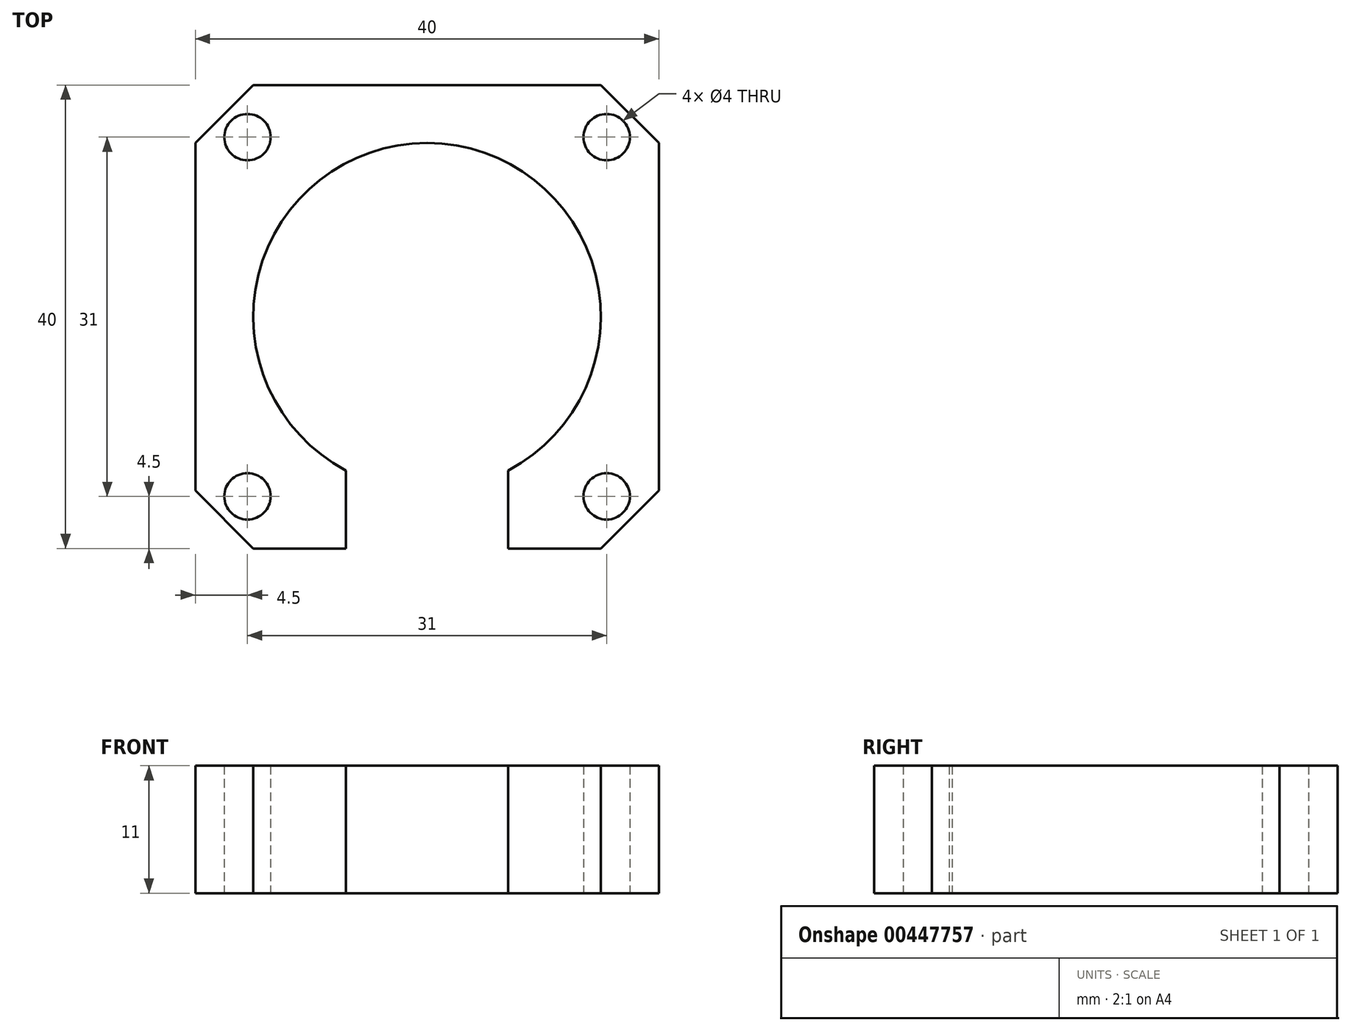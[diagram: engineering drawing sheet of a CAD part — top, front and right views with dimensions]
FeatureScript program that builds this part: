
annotation { "Feature Type Name" : "Feature", "Feature Type Description" : "" }
export const myFeature = defineFeature(function(context is Context, id is Id, definition is map)
    precondition{}
    {
        {
            var Q0;
            Q0=qCreatedBy(makeId("Top.planeOp"),FACE);
            var sketch = newSketch(context, id + "F0", { "sketchPlane" : qUnion([Q0])});
            skLineSegment(sketch, "E0.bottom", {"start": v(20, 20) * mm, "end": v(-20, 20) * mm});
            skLineSegment(sketch, "E0.top", {"start": v(20, -20) * mm, "end": v(-20, -20) * mm});
            skLineSegment(sketch, "E0.left", {"start": v(20, 20) * mm, "end": v(20, -20) * mm});
            skLineSegment(sketch, "E0.right", {"start": v(-20, 20) * mm, "end": v(-20, -20) * mm});
            skPoint(sketch, "E0.middle", {"position": v(0, 0) * mm});
            skCircle(sketch, "E1", {"center": v(15.5, 15.5) * mm, "radius": 2 * mm});
            skCircle(sketch, "E2", {"center": v(-15.5, 15.5) * mm, "radius": 2 * mm});
            skCircle(sketch, "E3", {"center": v(15.5, -15.5) * mm, "radius": 2 * mm});
            skCircle(sketch, "E4", {"center": v(-15.5, -15.5) * mm, "radius": 2 * mm});
            skCircle(sketch, "E5", {"center": v(0, 0) * mm, "radius": 15 * mm});
            skLineSegment(sketch, "E6", {"start": v(0, 0) * mm, "end": v(7, 0) * mm});
            skLineSegment(sketch, "E7", {"start": v(7, 0) * mm, "end": v(7, -20) * mm});
            skLineSegment(sketch, "E8", {"start": v(7, -20) * mm, "end": v(-7, -20) * mm});
            skLineSegment(sketch, "E9", {"start": v(-7, -20) * mm, "end": v(-7, 0) * mm});
            skLineSegment(sketch, "E10", {"start": v(-7, 0) * mm, "end": v(0, 0) * mm});
            skSolve(sketch);
        }
        {
            var Q0;
            Q0=makeQuery(id+"F0.imprint","IMPRINT",FACE,{"disambiguationData":[TD([[makeQuery(id+"F0.imprint","IMPRINT",EDGE,{"derivedFrom":sQuery(id+"F0.wireOp",EDGE,"E0.bottom")}),1.0]])]});
            extrude(context, id + "F1", {"entities" : qUnion([Q0]), "depth" : 11 * mm});
        }
        {
            var Q0;
            Q0=makeQuery(id+"F1.opExtrude","SWEPT_EDGE",EDGE,{"disambiguationData":[OSD([sQuery(id+"F0.wireOp",EDGE,"E0.top"),sQuery(id+"F0.wireOp",EDGE,"E0.right")])]});
            var Q1;
            Q1=makeQuery(id+"F1.opExtrude","SWEPT_EDGE",EDGE,{"disambiguationData":[OSD([sQuery(id+"F0.wireOp",EDGE,"E0.bottom"),sQuery(id+"F0.wireOp",EDGE,"E0.right")])]});
            var Q2;
            Q2=makeQuery(id+"F1.opExtrude","SWEPT_EDGE",EDGE,{"disambiguationData":[OSD([sQuery(id+"F0.wireOp",EDGE,"E0.bottom"),sQuery(id+"F0.wireOp",EDGE,"E0.left")])]});
            var Q3;
            Q3=makeQuery(id+"F1.opExtrude","SWEPT_EDGE",EDGE,{"disambiguationData":[OSD([sQuery(id+"F0.wireOp",EDGE,"E0.top"),sQuery(id+"F0.wireOp",EDGE,"E0.left")])]});
            chamfer(context, id + "F2", {"entities" : qUnion([Q0, Q1, Q2, Q3]), "width" : 5 * mm, "tangentPropagation" : true});
        }
    });
